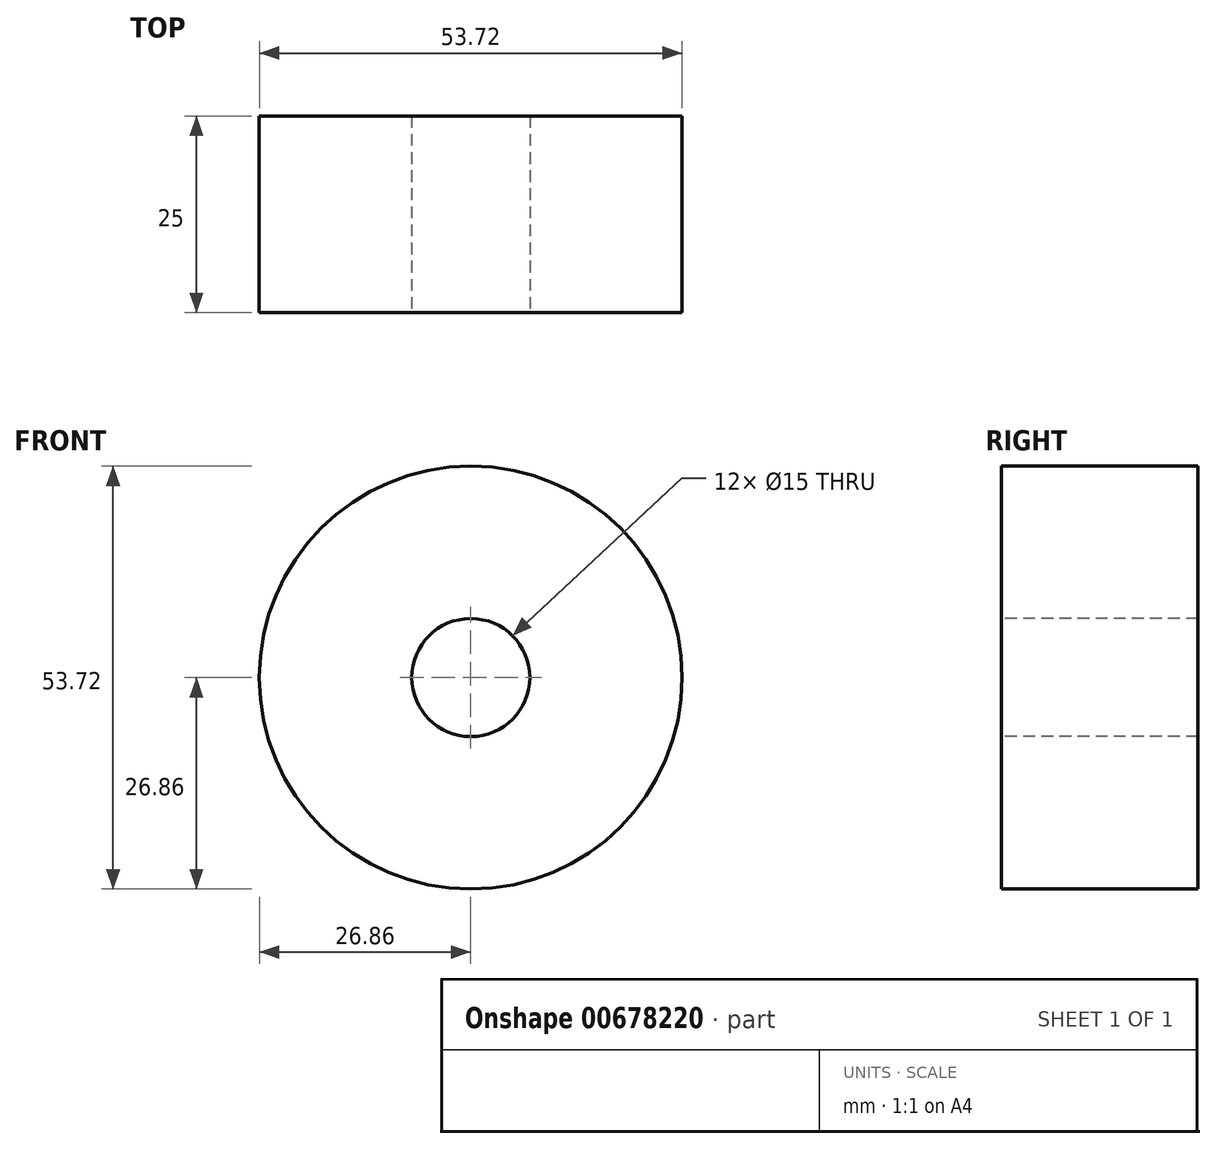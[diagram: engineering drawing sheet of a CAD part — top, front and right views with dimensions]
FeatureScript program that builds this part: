
annotation { "Feature Type Name" : "Feature", "Feature Type Description" : "" }
export const myFeature = defineFeature(function(context is Context, id is Id, definition is map)
    precondition{}
    {
        {
            var Q0;
            Q0=qCreatedBy(makeId("Front.planeOp"),FACE);
            var sketch = newSketch(context, id + "F0", { "sketchPlane" : qUnion([Q0])});
            skCircle(sketch, "E0", {"center": v(0, 0) * mm, "radius": 26.86 * mm});
            skCircle(sketch, "E1", {"center": v(0, 0) * mm, "radius": 27.57 * mm, "construction": true});
            skCircle(sketch, "E2", {"center": v(0, 0) * mm, "radius": 29.34 * mm, "construction": true});
            skCircle(sketch, "E3", {"center": v(0, 0) * mm, "radius": 31.75 * mm, "construction": true});
            skLineSegment(sketch, "E4", {"start": v(0, 0) * mm, "end": v(0, 45.75) * mm, "construction": true});
            skLineSegment(sketch, "E5", {"start": v(0, 0) * mm, "end": v(-2.9, 44.1) * mm, "construction": true});
            skCircle(sketch, "E6", {"center": v(0, 29.34) * mm, "radius": 14.6 * mm, "construction": true});
            skLineSegment(sketch, "E7", {"start": v(0, 29.34) * mm, "end": v(-52.03, 29.34) * mm, "construction": true});
            skArc(sketch, "E8.MirrorCS", {"start": v(-5.86, 30.73) * mm, "mid": v(-4.99, 33.38) * mm, "end": v(-3.65, 35.83) * mm});
            skArc(sketch, "E9.MirrorCS", {"start": v(-6.13, 26.15) * mm, "mid": v(-6.17, 28.45) * mm, "end": v(-5.86, 30.73) * mm});
            skArc(sketch, "E10.MirrorCS", {"start": v(1.8, 31.23) * mm, "mid": v(0.59, 33.75) * mm, "end": v(-1.06, 36) * mm});
            skArc(sketch, "E11.MirrorCS", {"start": v(2.67, 26.73) * mm, "mid": v(2.4, 29.01) * mm, "end": v(1.8, 31.23) * mm});
            skLineSegment(sketch, "E12", {"start": v(-3.65, 35.83) * mm, "end": v(-1.06, 36) * mm});
            skSolve(sketch);
        }
        {
            var Q0;
            {var subQ0=sQuery(id+"F0.wireOp",EDGE,"E0");var subQ1=makeQuery(id+"F0.imprint","INTERSECT",VERTEX,{"derivedFrom":[subQ0,sQuery(id+"F0.wireOp",EDGE,"E9.MirrorCS")]});Q0=makeQuery(id+"F0.imprint","IMPRINT",FACE,{"disambiguationData":[TD([[makeQuery(id+"F0.imprint","IMPRINT",EDGE,{"disambiguationData":[TD([[subQ1,1.0]])],"derivedFrom":subQ0}),1.0]])]});}
            var Q1;
            Q1=makeQuery(id+"F0.imprint","IMPRINT",FACE,{"disambiguationData":[TD([[makeQuery(id+"F0.imprint","IMPRINT",EDGE,{"derivedFrom":sQuery(id+"F0.wireOp",EDGE,"E8.MirrorCS")}),-1.0]])]});
            extrude(context, id + "F1", {"entities" : qUnion([Q0, Q1]), "depth" : 25 * mm, "offsetDistance" : 25 * mm});
        }
        {
            var Q0;
            Q0=makeQuery(id+"F1.opExtrude","SWEPT_BODY",BODY,{"disambiguationData":[OSD([sQuery(id+"F0.wireOp",EDGE,"E0"),sQuery(id+"F0.wireOp",EDGE,"E8.MirrorCS"),sQuery(id+"F0.wireOp",EDGE,"E9.MirrorCS"),sQuery(id+"F0.wireOp",EDGE,"5d9276b4-0de6-43f6-a04c-467d8c1ae6620.MirrorCS"),sQuery(id+"F0.wireOp",EDGE,"5d9276b4-0de6-43f6-a04c-467d8c1ae6621.MirrorCS"),sQuery(id+"F0.wireOp",EDGE,"dkYckQ6Z-mquH-0vGn-wuUz-jGdZaukbBRk5")])]});
            var Q1;
            Q1=makeQuery(id+"F1.opExtrude","SWEPT_FACE",FACE,{"disambiguationData":[OSD([sQuery(id+"F0.wireOp",EDGE,"E0")])]});
            circularPattern(context, id + "F2", {"entities" : qUnion([Q0]), "axis" : qUnion([Q1]), "angle" : 360 * degree, "instanceCount" : 12, "equalSpace" : true});
        }
        {
            var Q0;
            Q0=makeQuery(id+"F1.opExtrude","CAP_FACE",FACE,{"disambiguationData":[OSD([sQuery(id+"F0.wireOp",EDGE,"E0"),sQuery(id+"F0.wireOp",EDGE,"E8.MirrorCS"),sQuery(id+"F0.wireOp",EDGE,"E9.MirrorCS"),sQuery(id+"F0.wireOp",EDGE,"E10.MirrorCS"),sQuery(id+"F0.wireOp",EDGE,"E11.MirrorCS"),sQuery(id+"F0.wireOp",EDGE,"E12")])],"isStart":false});
            var sketch = newSketch(context, id + "F3", { "sketchPlane" : qUnion([Q0])});
            skCircle(sketch, "E13", {"center": v(0, 0) * mm, "radius": 8.45 * mm});
            skSolve(sketch);
        }
        {
            var Q0;
            Q0=sQuery(id+"F3.wireOp",VERTEX,"E13.center");
            var Q1;
            Q1=makeQuery(id+"F1.opExtrude","SWEPT_BODY",BODY,{"disambiguationData":[OSD([sQuery(id+"F0.wireOp",EDGE,"E0"),sQuery(id+"F0.wireOp",EDGE,"E8.MirrorCS"),sQuery(id+"F0.wireOp",EDGE,"E9.MirrorCS"),sQuery(id+"F0.wireOp",EDGE,"E10.MirrorCS"),sQuery(id+"F0.wireOp",EDGE,"E11.MirrorCS"),sQuery(id+"F0.wireOp",EDGE,"E12")])]});
            var Q2;
            Q2=makeQuery(id+"F2.opPattern","COPY",BODY,{"derivedFrom":makeQuery(id+"F1.opExtrude","SWEPT_BODY",BODY,{"disambiguationData":[OSD([sQuery(id+"F0.wireOp",EDGE,"E0"),sQuery(id+"F0.wireOp",EDGE,"E8.MirrorCS"),sQuery(id+"F0.wireOp",EDGE,"E9.MirrorCS"),sQuery(id+"F0.wireOp",EDGE,"E10.MirrorCS"),sQuery(id+"F0.wireOp",EDGE,"E11.MirrorCS"),sQuery(id+"F0.wireOp",EDGE,"E12")])]}),"instanceName":"1"});
            var Q3;
            Q3=makeQuery(id+"F2.opPattern","COPY",BODY,{"derivedFrom":makeQuery(id+"F1.opExtrude","SWEPT_BODY",BODY,{"disambiguationData":[OSD([sQuery(id+"F0.wireOp",EDGE,"E0"),sQuery(id+"F0.wireOp",EDGE,"E8.MirrorCS"),sQuery(id+"F0.wireOp",EDGE,"E9.MirrorCS"),sQuery(id+"F0.wireOp",EDGE,"E10.MirrorCS"),sQuery(id+"F0.wireOp",EDGE,"E11.MirrorCS"),sQuery(id+"F0.wireOp",EDGE,"E12")])]}),"instanceName":"2"});
            var Q4;
            Q4=makeQuery(id+"F2.opPattern","COPY",BODY,{"derivedFrom":makeQuery(id+"F1.opExtrude","SWEPT_BODY",BODY,{"disambiguationData":[OSD([sQuery(id+"F0.wireOp",EDGE,"E0"),sQuery(id+"F0.wireOp",EDGE,"E8.MirrorCS"),sQuery(id+"F0.wireOp",EDGE,"E9.MirrorCS"),sQuery(id+"F0.wireOp",EDGE,"E10.MirrorCS"),sQuery(id+"F0.wireOp",EDGE,"E11.MirrorCS"),sQuery(id+"F0.wireOp",EDGE,"E12")])]}),"instanceName":"3"});
            var Q5;
            Q5=makeQuery(id+"F2.opPattern","COPY",BODY,{"derivedFrom":makeQuery(id+"F1.opExtrude","SWEPT_BODY",BODY,{"disambiguationData":[OSD([sQuery(id+"F0.wireOp",EDGE,"E0"),sQuery(id+"F0.wireOp",EDGE,"E8.MirrorCS"),sQuery(id+"F0.wireOp",EDGE,"E9.MirrorCS"),sQuery(id+"F0.wireOp",EDGE,"E10.MirrorCS"),sQuery(id+"F0.wireOp",EDGE,"E11.MirrorCS"),sQuery(id+"F0.wireOp",EDGE,"E12")])]}),"instanceName":"4"});
            var Q6;
            Q6=makeQuery(id+"F2.opPattern","COPY",BODY,{"derivedFrom":makeQuery(id+"F1.opExtrude","SWEPT_BODY",BODY,{"disambiguationData":[OSD([sQuery(id+"F0.wireOp",EDGE,"E0"),sQuery(id+"F0.wireOp",EDGE,"E8.MirrorCS"),sQuery(id+"F0.wireOp",EDGE,"E9.MirrorCS"),sQuery(id+"F0.wireOp",EDGE,"E10.MirrorCS"),sQuery(id+"F0.wireOp",EDGE,"E11.MirrorCS"),sQuery(id+"F0.wireOp",EDGE,"E12")])]}),"instanceName":"5"});
            var Q7;
            Q7=makeQuery(id+"F2.opPattern","COPY",BODY,{"derivedFrom":makeQuery(id+"F1.opExtrude","SWEPT_BODY",BODY,{"disambiguationData":[OSD([sQuery(id+"F0.wireOp",EDGE,"E0"),sQuery(id+"F0.wireOp",EDGE,"E8.MirrorCS"),sQuery(id+"F0.wireOp",EDGE,"E9.MirrorCS"),sQuery(id+"F0.wireOp",EDGE,"E10.MirrorCS"),sQuery(id+"F0.wireOp",EDGE,"E11.MirrorCS"),sQuery(id+"F0.wireOp",EDGE,"E12")])]}),"instanceName":"6"});
            var Q8;
            Q8=makeQuery(id+"F2.opPattern","COPY",BODY,{"derivedFrom":makeQuery(id+"F1.opExtrude","SWEPT_BODY",BODY,{"disambiguationData":[OSD([sQuery(id+"F0.wireOp",EDGE,"E0"),sQuery(id+"F0.wireOp",EDGE,"E8.MirrorCS"),sQuery(id+"F0.wireOp",EDGE,"E9.MirrorCS"),sQuery(id+"F0.wireOp",EDGE,"E10.MirrorCS"),sQuery(id+"F0.wireOp",EDGE,"E11.MirrorCS"),sQuery(id+"F0.wireOp",EDGE,"E12")])]}),"instanceName":"7"});
            var Q9;
            Q9=makeQuery(id+"F2.opPattern","COPY",BODY,{"derivedFrom":makeQuery(id+"F1.opExtrude","SWEPT_BODY",BODY,{"disambiguationData":[OSD([sQuery(id+"F0.wireOp",EDGE,"E0"),sQuery(id+"F0.wireOp",EDGE,"E8.MirrorCS"),sQuery(id+"F0.wireOp",EDGE,"E9.MirrorCS"),sQuery(id+"F0.wireOp",EDGE,"E10.MirrorCS"),sQuery(id+"F0.wireOp",EDGE,"E11.MirrorCS"),sQuery(id+"F0.wireOp",EDGE,"E12")])]}),"instanceName":"8"});
            var Q10;
            Q10=makeQuery(id+"F2.opPattern","COPY",BODY,{"derivedFrom":makeQuery(id+"F1.opExtrude","SWEPT_BODY",BODY,{"disambiguationData":[OSD([sQuery(id+"F0.wireOp",EDGE,"E0"),sQuery(id+"F0.wireOp",EDGE,"E8.MirrorCS"),sQuery(id+"F0.wireOp",EDGE,"E9.MirrorCS"),sQuery(id+"F0.wireOp",EDGE,"E10.MirrorCS"),sQuery(id+"F0.wireOp",EDGE,"E11.MirrorCS"),sQuery(id+"F0.wireOp",EDGE,"E12")])]}),"instanceName":"9"});
            var Q11;
            Q11=makeQuery(id+"F2.opPattern","COPY",BODY,{"derivedFrom":makeQuery(id+"F1.opExtrude","SWEPT_BODY",BODY,{"disambiguationData":[OSD([sQuery(id+"F0.wireOp",EDGE,"E0"),sQuery(id+"F0.wireOp",EDGE,"E8.MirrorCS"),sQuery(id+"F0.wireOp",EDGE,"E9.MirrorCS"),sQuery(id+"F0.wireOp",EDGE,"E10.MirrorCS"),sQuery(id+"F0.wireOp",EDGE,"E11.MirrorCS"),sQuery(id+"F0.wireOp",EDGE,"E12")])]}),"instanceName":"10"});
            var Q12;
            Q12=makeQuery(id+"F2.opPattern","COPY",BODY,{"derivedFrom":makeQuery(id+"F1.opExtrude","SWEPT_BODY",BODY,{"disambiguationData":[OSD([sQuery(id+"F0.wireOp",EDGE,"E0"),sQuery(id+"F0.wireOp",EDGE,"E8.MirrorCS"),sQuery(id+"F0.wireOp",EDGE,"E9.MirrorCS"),sQuery(id+"F0.wireOp",EDGE,"E10.MirrorCS"),sQuery(id+"F0.wireOp",EDGE,"E11.MirrorCS"),sQuery(id+"F0.wireOp",EDGE,"E12")])]}),"instanceName":"11"});
            hole(context, id + "F4", {"style" : HoleStyle.SIMPLE, "endStyle" : HoleEndStyle.THROUGH, "holeDiameter" : 15 * mm, "majorDiameter" : 5 * mm, "isTappedThrough" : true, "tappedDepth" : 12 * mm, "tapClearance" : 3, "locations" : qUnion([Q0]), "scope" : qUnion([Q1, Q2, Q3, Q4, Q5, Q6, Q7, Q8, Q9, Q10, Q11, Q12])});
        }
    });
